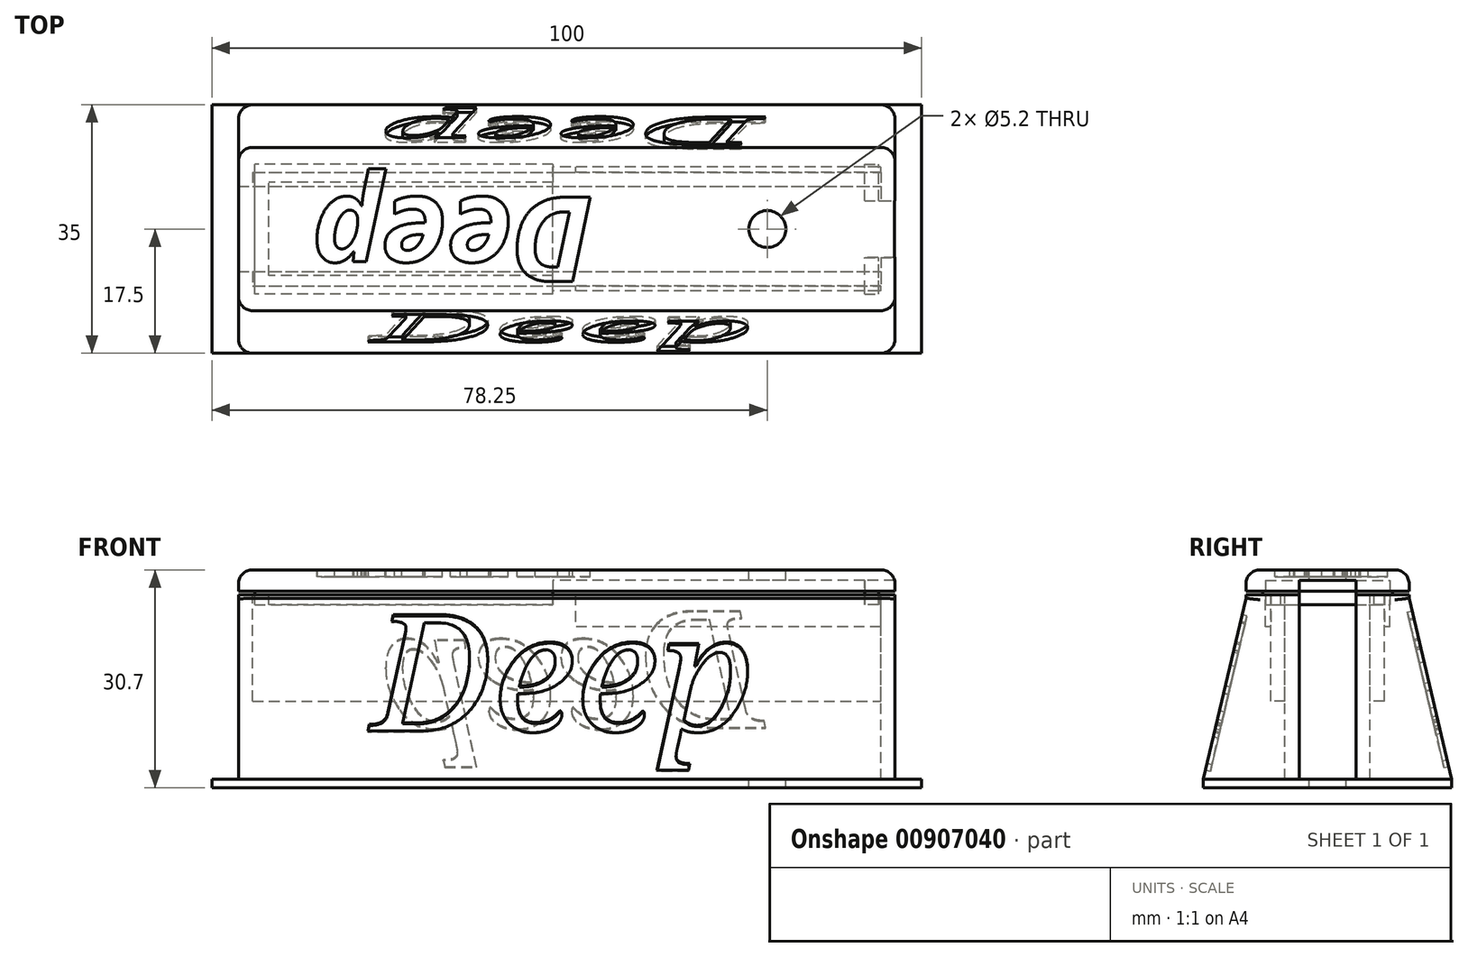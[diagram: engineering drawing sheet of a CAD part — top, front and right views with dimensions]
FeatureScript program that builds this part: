
annotation { "Feature Type Name" : "Feature", "Feature Type Description" : "" }
export const myFeature = defineFeature(function(context is Context, id is Id, definition is map)
    precondition{}
    {
        {
            var Q0;
            Q0=qCreatedBy(makeId("Top.planeOp"),FACE);
            var sketch = newSketch(context, id + "F0", { "sketchPlane" : qUnion([Q0])});
            skLineSegment(sketch, "E0.bottom", {"start": v(-50, 17.5) * mm, "end": v(50, 17.5) * mm});
            skLineSegment(sketch, "E0.top", {"start": v(-50, -17.5) * mm, "end": v(50, -17.5) * mm});
            skLineSegment(sketch, "E0.left", {"start": v(-50, 17.5) * mm, "end": v(-50, -17.5) * mm});
            skLineSegment(sketch, "E0.right", {"start": v(50, 17.5) * mm, "end": v(50, -17.5) * mm});
            skSolve(sketch);
        }
        {
            var Q0;
            Q0=makeQuery(id+"F0.imprint","IMPRINT",FACE,{"disambiguationData":[TD([[makeQuery(id+"F0.imprint","IMPRINT",EDGE,{"derivedFrom":sQuery(id+"F0.wireOp",EDGE,"E0.bottom")}),-1.0]])]});
            extrude(context, id + "F1", {"entities" : qUnion([Q0]), "depth" : 1.2 * mm, "offsetDistance" : 25 * mm});
        }
        {
            var Q0;
            Q0=makeQuery(id+"F1.opExtrude","CAP_FACE",FACE,{"disambiguationData":[OSD([sQuery(id+"F0.wireOp",EDGE,"E0.bottom"),sQuery(id+"F0.wireOp",EDGE,"E0.top"),sQuery(id+"F0.wireOp",EDGE,"E0.left"),sQuery(id+"F0.wireOp",EDGE,"E0.right")])],"isStart":false});
            var sketch = newSketch(context, id + "F2", { "sketchPlane" : qUnion([Q0])});
            skLineSegment(sketch, "E1.bottom", {"start": v(-46.25, 11.5) * mm, "end": v(46.25, 11.5) * mm});
            skLineSegment(sketch, "E1.top", {"start": v(-46.25, -11.5) * mm, "end": v(46.25, -11.5) * mm});
            skLineSegment(sketch, "E1.left", {"start": v(-46.25, 11.5) * mm, "end": v(-46.25, -11.5) * mm});
            skLineSegment(sketch, "E1.right", {"start": v(46.25, 11.5) * mm, "end": v(46.25, -11.5) * mm});
            skSolve(sketch);
        }
        {
            var Q0;
            Q0=makeQuery(id+"F2.imprint","IMPRINT",FACE,{"disambiguationData":[TD([[makeQuery(id+"F2.imprint","IMPRINT",EDGE,{"derivedFrom":sQuery(id+"F2.wireOp",EDGE,"E1.bottom")}),-1.0]])]});
            extrude(context, id + "F3", {"entities" : qUnion([Q0]), "operationType" : NewBodyOperationType.ADD, "depth" : 26 * mm, "offsetDistance" : 25 * mm});
        }
        {
            var Q0;
            Q0=makeQuery(id+"F3.opExtrude","SWEPT_FACE",FACE,{"disambiguationData":[OSD([sQuery(id+"F2.wireOp",EDGE,"E1.left")])]});
            var sketch = newSketch(context, id + "F4", { "sketchPlane" : qUnion([Q0])});
            skLineSegment(sketch, "E2", {"start": v(-11.5, 26.7) * mm, "end": v(-11.5, 1.2) * mm});
            skLineSegment(sketch, "E3", {"start": v(-11.5, 1.2) * mm, "end": v(-17.5, 1.2) * mm});
            skLineSegment(sketch, "E4", {"start": v(-17.5, 1.2) * mm, "end": v(-11.5, 26.7) * mm});
            skLineSegment(sketch, "E5", {"start": v(11.5, 26.7) * mm, "end": v(11.5, 1.2) * mm});
            skLineSegment(sketch, "E6", {"start": v(11.5, 1.2) * mm, "end": v(17.5, 1.2) * mm});
            skLineSegment(sketch, "E7", {"start": v(17.5, 1.2) * mm, "end": v(11.5, 26.7) * mm});
            skSolve(sketch);
        }
        {
            var Q0;
            Q0=makeQuery(id+"F4.imprint","IMPRINT",FACE,{"disambiguationData":[TD([[makeQuery(id+"F4.imprint","IMPRINT",EDGE,{"derivedFrom":sQuery(id+"F4.wireOp",EDGE,"E2")}),-1.0]])]});
            var Q1;
            Q1=makeQuery(id+"F4.imprint","IMPRINT",FACE,{"disambiguationData":[TD([[makeQuery(id+"F4.imprint","IMPRINT",EDGE,{"derivedFrom":sQuery(id+"F4.wireOp",EDGE,"E5")}),1.0]])]});
            extrude(context, id + "F5", {"entities" : qUnion([Q0, Q1]), "operationType" : NewBodyOperationType.ADD, "oppositeDirection" : true, "depth" : 92.5 * mm, "offsetDistance" : 25 * mm});
        }
        {
            var Q0;
            Q0=makeQuery(id+"F3.opExtrude","CAP_FACE",FACE,{"disambiguationData":[OSD([sQuery(id+"F2.wireOp",EDGE,"E1.bottom"),sQuery(id+"F2.wireOp",EDGE,"E1.top"),sQuery(id+"F2.wireOp",EDGE,"E1.left"),sQuery(id+"F2.wireOp",EDGE,"E1.right")])],"isStart":false});
            var sketch = newSketch(context, id + "F6", { "sketchPlane" : qUnion([Q0])});
            skLineSegment(sketch, "E8.bottom", {"start": v(-44.25, 8) * mm, "end": v(44.25, 8) * mm});
            skLineSegment(sketch, "E8.top", {"start": v(-44.25, -8) * mm, "end": v(44.25, -8) * mm});
            skLineSegment(sketch, "E8.left", {"start": v(-44.25, 8) * mm, "end": v(-44.25, -8) * mm});
            skLineSegment(sketch, "E8.right", {"start": v(44.25, 8) * mm, "end": v(44.25, -8) * mm});
            skSolve(sketch);
        }
        {
            var Q0;
            Q0=makeQuery(id+"F6.imprint","IMPRINT",FACE,{"disambiguationData":[TD([[makeQuery(id+"F6.imprint","IMPRINT",EDGE,{"derivedFrom":sQuery(id+"F6.wireOp",EDGE,"E8.bottom")}),-1.0]])]});
            extrude(context, id + "F7", {"entities" : qUnion([Q0]), "operationType" : NewBodyOperationType.REMOVE, "oppositeDirection" : true, "depth" : 15 * mm, "offsetDistance" : 25 * mm});
        }
        {
            var Q0;
            Q0=makeQuery(id+"F7.boolean.opBoolean","COPY",FACE,{"derivedFrom":makeQuery(id+"F7.opExtrude","CAP_FACE",FACE,{"disambiguationData":[OSD([sQuery(id+"F6.wireOp",EDGE,"E8.bottom"),sQuery(id+"F6.wireOp",EDGE,"E8.top"),sQuery(id+"F6.wireOp",EDGE,"E8.left"),sQuery(id+"F6.wireOp",EDGE,"E8.right")])],"isStart":false})});
            var sketch = newSketch(context, id + "F8", { "sketchPlane" : qUnion([Q0])});
            skLineSegment(sketch, "E9.bottom", {"start": v(-44.25, 6) * mm, "end": v(44.25, 6) * mm});
            skLineSegment(sketch, "E9.top", {"start": v(-44.25, -6) * mm, "end": v(44.25, -6) * mm});
            skLineSegment(sketch, "E9.left", {"start": v(-44.25, 6) * mm, "end": v(-44.25, -6) * mm});
            skLineSegment(sketch, "E9.right", {"start": v(44.25, 6) * mm, "end": v(44.25, -6) * mm});
            skSolve(sketch);
        }
        {
            var Q0;
            Q0=makeQuery(id+"F8.imprint","IMPRINT",FACE,{"disambiguationData":[TD([[makeQuery(id+"F8.imprint","IMPRINT",EDGE,{"derivedFrom":sQuery(id+"F8.wireOp",EDGE,"E9.bottom")}),-1.0]])]});
            extrude(context, id + "F9", {"entities" : qUnion([Q0]), "operationType" : NewBodyOperationType.REMOVE, "oppositeDirection" : true, "depth" : 11 * mm, "offsetDistance" : 25 * mm});
        }
        {
            var Q0;
            Q0=makeQuery(id+"F3.opExtrude","CAP_FACE",FACE,{"disambiguationData":[OSD([sQuery(id+"F2.wireOp",EDGE,"E1.bottom"),sQuery(id+"F2.wireOp",EDGE,"E1.top"),sQuery(id+"F2.wireOp",EDGE,"E1.left"),sQuery(id+"F2.wireOp",EDGE,"E1.right")])],"isStart":false});
            var sketch = newSketch(context, id + "F10", { "sketchPlane" : qUnion([Q0])});
            skLineSegment(sketch, "E10.bottom", {"start": v(44.25, 4) * mm, "end": v(46.25, 4) * mm});
            skLineSegment(sketch, "E10.top", {"start": v(44.25, -4) * mm, "end": v(46.25, -4) * mm});
            skLineSegment(sketch, "E10.left", {"start": v(44.25, 4) * mm, "end": v(44.25, -4) * mm});
            skLineSegment(sketch, "E10.right", {"start": v(46.25, 4) * mm, "end": v(46.25, -4) * mm});
            skSolve(sketch);
        }
        {
            var Q0;
            Q0=makeQuery(id+"F10.imprint","IMPRINT",FACE,{"disambiguationData":[TD([[makeQuery(id+"F10.imprint","IMPRINT",EDGE,{"derivedFrom":sQuery(id+"F10.wireOp",EDGE,"E10.bottom")}),-1.0]])]});
            extrude(context, id + "F11", {"entities" : qUnion([Q0]), "operationType" : NewBodyOperationType.REMOVE, "oppositeDirection" : true, "depth" : 26 * mm, "offsetDistance" : 25 * mm});
        }
        {
            var Q0;
            Q0=makeQuery(id+"F3.opExtrude","CAP_FACE",FACE,{"disambiguationData":[OSD([sQuery(id+"F2.wireOp",EDGE,"E1.bottom"),sQuery(id+"F2.wireOp",EDGE,"E1.top"),sQuery(id+"F2.wireOp",EDGE,"E1.left"),sQuery(id+"F2.wireOp",EDGE,"E1.right")])],"isStart":false});
            var sketch = newSketch(context, id + "F12", { "sketchPlane" : qUnion([Q0])});
            skLineSegment(sketch, "E11.bottom", {"start": v(-46.25, 6) * mm, "end": v(-44.25, 6) * mm});
            skLineSegment(sketch, "E11.top", {"start": v(-46.25, -6) * mm, "end": v(-44.25, -6) * mm});
            skLineSegment(sketch, "E11.left", {"start": v(-46.25, 6) * mm, "end": v(-46.25, -6) * mm});
            skLineSegment(sketch, "E11.right", {"start": v(-44.25, 6) * mm, "end": v(-44.25, -6) * mm});
            skSolve(sketch);
        }
        {
            var Q0;
            Q0=makeQuery(id+"F12.imprint","IMPRINT",FACE,{"disambiguationData":[TD([[makeQuery(id+"F12.imprint","IMPRINT",EDGE,{"derivedFrom":sQuery(id+"F12.wireOp",EDGE,"E11.bottom")}),-1.0]])]});
            extrude(context, id + "F13", {"entities" : qUnion([Q0]), "operationType" : NewBodyOperationType.REMOVE, "oppositeDirection" : true, "depth" : 26 * mm, "offsetDistance" : 25 * mm});
        }
        {
            var Q0;
            {var subQ0=sQuery(id+"F2.wireOp",EDGE,"E1.right");var subQ1=sQuery(id+"F2.wireOp",EDGE,"E1.left");var subQ2=sQuery(id+"F2.wireOp",EDGE,"E1.top");Q0=makeQuery(id+"F13.boolean.opBoolean","SPLIT",FACE,{"disambiguationData":[TD([makeQuery(id+"F3.opExtrude","SWEPT_FACE",FACE,{"disambiguationData":[OSD([subQ2])]})])],"derivedFrom":makeQuery(id+"F3.opExtrude","CAP_FACE",FACE,{"disambiguationData":[OSD([sQuery(id+"F2.wireOp",EDGE,"E1.bottom"),subQ2,subQ1,subQ0])],"isStart":false})});}
            var sketch = newSketch(context, id + "F14", { "sketchPlane" : qUnion([Q0])});
            skLineSegment(sketch, "E12.bottom", {"start": v(44.23, -8.75) * mm, "end": v(1.23, -8.75) * mm});
            skLineSegment(sketch, "E12.top", {"start": v(44.23, 8.75) * mm, "end": v(1.23, 8.75) * mm});
            skLineSegment(sketch, "E12.left", {"start": v(44.23, 8.75) * mm, "end": v(44.23, -8.75) * mm});
            skLineSegment(sketch, "E12.right", {"start": v(1.23, 8.75) * mm, "end": v(1.23, -8.75) * mm});
            skSolve(sketch);
        }
        {
            var Q0;
            Q0=makeQuery(id+"F14.imprint","IMPRINT",FACE,{"disambiguationData":[TD([[makeQuery(id+"F14.imprint","IMPRINT",EDGE,{"derivedFrom":sQuery(id+"F14.wireOp",EDGE,"E12.bottom")}),-1.0]])]});
            var Q1;
            {var subQ0=sQuery(id+"F14.wireOp",EDGE,"E12.top");Q1=makeQuery(id+"F14.imprint","IMPRINT",FACE,{"disambiguationData":[TD([[makeQuery(id+"F14.imprint","IMPRINT",EDGE,{"derivedFrom":subQ0}),1.0]])]});}
            extrude(context, id + "F15", {"entities" : qUnion([Q0, Q1]), "operationType" : NewBodyOperationType.REMOVE, "oppositeDirection" : true, "depth" : 4.5 * mm, "offsetDistance" : 25 * mm});
        }
        {
            var Q0;
            {var subQ0=sQuery(id+"F2.wireOp",EDGE,"E1.left");var subQ1=sQuery(id+"F2.wireOp",EDGE,"E1.right");var subQ2=sQuery(id+"F2.wireOp",EDGE,"E1.bottom");Q0=makeQuery(id+"F13.boolean.opBoolean","SPLIT",FACE,{"disambiguationData":[TD([makeQuery(id+"F3.opExtrude","SWEPT_FACE",FACE,{"disambiguationData":[OSD([subQ2])]})])],"derivedFrom":makeQuery(id+"F3.opExtrude","CAP_FACE",FACE,{"disambiguationData":[OSD([subQ2,sQuery(id+"F2.wireOp",EDGE,"E1.top"),subQ0,subQ1])],"isStart":false})});}
            cPlane(context, id + "F16", {"entities" : qUnion([Q0]), "cplaneType" : CPlaneType.OFFSET, "offset" : .5 * mm, "width" : 150 * mm, "height" : 150 * mm});
        }
        {
            var Q0;
            Q0=qCreatedBy(id+"F16.planeOp",FACE);
            var sketch = newSketch(context, id + "F17", { "sketchPlane" : qUnion([Q0])});
            skLineSegment(sketch, "E13.bottom", {"start": v(-46.25, 11.5) * mm, "end": v(46.25, 11.5) * mm});
            skLineSegment(sketch, "E13.top", {"start": v(-46.25, -11.5) * mm, "end": v(46.25, -11.5) * mm});
            skLineSegment(sketch, "E13.left", {"start": v(-46.25, 11.5) * mm, "end": v(-46.25, -11.5) * mm});
            skLineSegment(sketch, "E13.right", {"start": v(46.25, 11.5) * mm, "end": v(46.25, -11.5) * mm});
            skSolve(sketch);
        }
        {
            var Q0;
            Q0=makeQuery(id+"F17.imprint","IMPRINT",FACE,{"disambiguationData":[TD([[makeQuery(id+"F17.imprint","IMPRINT",EDGE,{"derivedFrom":sQuery(id+"F17.wireOp",EDGE,"E13.bottom")}),-1.0]])]});
            extrude(context, id + "F18", {"entities" : qUnion([Q0]), "depth" : 3 * mm, "offsetDistance" : 25 * mm});
        }
        {
            var Q0;
            Q0=makeQuery(id+"F18.opExtrude","SWEPT_EDGE",EDGE,{"disambiguationData":[OSD([sQuery(id+"F17.wireOp",EDGE,"E13.top"),sQuery(id+"F17.wireOp",EDGE,"E13.left")])]});
            var Q1;
            Q1=makeQuery(id+"F18.opExtrude","CAP_EDGE",EDGE,{"disambiguationData":[OSD([sQuery(id+"F17.wireOp",EDGE,"E13.left")])],"isStart":false});
            var Q2;
            Q2=makeQuery(id+"F18.opExtrude","CAP_EDGE",EDGE,{"disambiguationData":[OSD([sQuery(id+"F17.wireOp",EDGE,"E13.top")])],"isStart":false});
            var Q3;
            Q3=makeQuery(id+"F18.opExtrude","SWEPT_EDGE",EDGE,{"disambiguationData":[OSD([sQuery(id+"F17.wireOp",EDGE,"E13.top"),sQuery(id+"F17.wireOp",EDGE,"E13.right")])]});
            var Q4;
            Q4=makeQuery(id+"F18.opExtrude","CAP_EDGE",EDGE,{"disambiguationData":[OSD([sQuery(id+"F17.wireOp",EDGE,"E13.right")])],"isStart":false});
            var Q5;
            Q5=makeQuery(id+"F18.opExtrude","SWEPT_EDGE",EDGE,{"disambiguationData":[OSD([sQuery(id+"F17.wireOp",EDGE,"E13.bottom"),sQuery(id+"F17.wireOp",EDGE,"E13.right")])]});
            var Q6;
            Q6=makeQuery(id+"F18.opExtrude","CAP_EDGE",EDGE,{"disambiguationData":[OSD([sQuery(id+"F17.wireOp",EDGE,"E13.bottom")])],"isStart":false});
            var Q7;
            Q7=makeQuery(id+"F18.opExtrude","SWEPT_EDGE",EDGE,{"disambiguationData":[OSD([sQuery(id+"F17.wireOp",EDGE,"E13.bottom"),sQuery(id+"F17.wireOp",EDGE,"E13.left")])]});
            fillet(context, id + "F19", {"entities" : qUnion([Q0, Q1, Q2, Q3, Q4, Q5, Q6, Q7]), "radius" : 2 * mm, "tangentPropagation" : true, "allowEdgeOverflow" : false});
        }
        {
            var Q0;
            Q0=makeQuery(id+"F5.opExtrude","SWEPT_FACE",FACE,{"disambiguationData":[OSD([sQuery(id+"F4.wireOp",EDGE,"E7")])]});
            var sketch = newSketch(context, id + "F20", { "sketchPlane" : qUnion([Q0])});
            skText(sketch, "E14", { "text": "Deep", "fontName": "NotoSerif-Italic.ttf"});
            const initialGuessF20  = {"E14": [-0.0275, 0.00413, 1, 0, 0.01699]};
            skSetInitialGuess(sketch, initialGuessF20);
            skSolve(sketch);
        }
        {
            var Q0;
            Q0 = qSketchRegion(id + "F20", true);
            extrude(context, id + "F21", {"entities" : qUnion([Q0]), "operationType" : NewBodyOperationType.REMOVE, "oppositeDirection" : true, "depth" : .7 * mm, "offsetDistance" : 25 * mm});
        }
        {
            var Q0;
            Q0=makeQuery(id+"F5.opExtrude","SWEPT_FACE",FACE,{"disambiguationData":[OSD([sQuery(id+"F4.wireOp",EDGE,"E4")])]});
            var sketch = newSketch(context, id + "F22", { "sketchPlane" : qUnion([Q0])});
            skText(sketch, "E15", { "text": "Deep", "fontName": "NotoSerif-Italic.ttf"});
            const initialGuessF22  = {"E15": [-0.0275, 0.00468, 1, 0, 0.01699]};
            skSetInitialGuess(sketch, initialGuessF22);
            skSolve(sketch);
        }
        {
            var Q0;
            Q0 = qSketchRegion(id + "F22", true);
            extrude(context, id + "F23", {"entities" : qUnion([Q0]), "operationType" : NewBodyOperationType.REMOVE, "oppositeDirection" : true, "depth" : .7 * mm, "offsetDistance" : 25 * mm});
        }
        {
            var Q0;
            Q0=makeQuery(id+"F5.opExtrude","CAP_EDGE",EDGE,{"disambiguationData":[OSD([sQuery(id+"F4.wireOp",EDGE,"E4")])],"isStart":false});
            var Q1;
            Q1=makeQuery(id+"F5.opExtrude","CAP_EDGE",EDGE,{"disambiguationData":[OSD([sQuery(id+"F4.wireOp",EDGE,"E7")])],"isStart":false});
            var Q2;
            Q2=makeQuery(id+"F5.opExtrude","CAP_EDGE",EDGE,{"disambiguationData":[OSD([sQuery(id+"F4.wireOp",EDGE,"E7")])],"isStart":true});
            var Q3;
            Q3=makeQuery(id+"F5.opExtrude","CAP_EDGE",EDGE,{"disambiguationData":[OSD([sQuery(id+"F4.wireOp",EDGE,"E4")])],"isStart":true});
            var Q4;
            Q4=makeQuery(id+"F3.opExtrude","SWEPT_EDGE",EDGE,{"disambiguationData":[OSD([sQuery(id+"F2.wireOp",EDGE,"E1.bottom"),sQuery(id+"F2.wireOp",EDGE,"E1.right")])]});
            var Q5;
            Q5=makeQuery(id+"F3.opExtrude","SWEPT_EDGE",EDGE,{"disambiguationData":[OSD([sQuery(id+"F2.wireOp",EDGE,"E1.top"),sQuery(id+"F2.wireOp",EDGE,"E1.right")])]});
            var Q6;
            Q6=makeQuery(id+"F3.opExtrude","SWEPT_EDGE",EDGE,{"disambiguationData":[OSD([sQuery(id+"F2.wireOp",EDGE,"E1.top"),sQuery(id+"F2.wireOp",EDGE,"E1.left")])]});
            var Q7;
            Q7=makeQuery(id+"F3.opExtrude","SWEPT_EDGE",EDGE,{"disambiguationData":[OSD([sQuery(id+"F2.wireOp",EDGE,"E1.bottom"),sQuery(id+"F2.wireOp",EDGE,"E1.left")])]});
            fillet(context, id + "F24", {"entities" : qUnion([Q0, Q1, Q2, Q3, Q4, Q5, Q6, Q7]), "radius" : 2 * mm, "tangentPropagation" : true, "allowEdgeOverflow" : false});
        }
        {
            var Q0;
            Q0=makeQuery(id+"F18.opExtrude","CAP_FACE",FACE,{"disambiguationData":[OSD([sQuery(id+"F17.wireOp",EDGE,"E13.bottom"),sQuery(id+"F17.wireOp",EDGE,"E13.top"),sQuery(id+"F17.wireOp",EDGE,"E13.left"),sQuery(id+"F17.wireOp",EDGE,"E13.right")])],"isStart":true});
            var sketch = newSketch(context, id + "F25", { "sketchPlane" : qUnion([Q0])});
            skLineSegment(sketch, "E16.bottom", {"start": v(41.95, 9.15) * mm, "end": v(43.95, 9.15) * mm});
            skLineSegment(sketch, "E16.top", {"start": v(41.95, 4) * mm, "end": v(43.95, 4) * mm});
            skLineSegment(sketch, "E16.left", {"start": v(41.95, 9.15) * mm, "end": v(41.95, 4) * mm});
            skLineSegment(sketch, "E16.right", {"start": v(43.95, 9.15) * mm, "end": v(43.95, 4) * mm});
            skLineSegment(sketch, "E17.bottom", {"start": v(41.95, -4) * mm, "end": v(43.95, -4) * mm});
            skLineSegment(sketch, "E17.top", {"start": v(41.95, -9.15) * mm, "end": v(43.95, -9.15) * mm});
            skLineSegment(sketch, "E17.left", {"start": v(41.95, -4) * mm, "end": v(41.95, -9.15) * mm});
            skLineSegment(sketch, "E17.right", {"start": v(43.95, -4) * mm, "end": v(43.95, -9.15) * mm});
            skPoint(sketch, "E18.oppositeSnap0", {"position": v(41.95, 6.57) * mm});
            skLineSegment(sketch, "E18.bottom", {"start": v(-1.95, 9.15) * mm, "end": v(-43.95, 9.15) * mm});
            skLineSegment(sketch, "E18.top", {"start": v(-1.95, 6.57) * mm, "end": v(-43.95, 6.57) * mm});
            skLineSegment(sketch, "E18.left", {"start": v(-1.95, 9.15) * mm, "end": v(-1.95, 6.57) * mm});
            skLineSegment(sketch, "E18.right", {"start": v(-43.95, 9.15) * mm, "end": v(-43.95, 6.57) * mm});
            skPoint(sketch, "E19.oppositeSnap0", {"position": v(43.95, -6.57) * mm});
            skLineSegment(sketch, "E19.bottom", {"start": v(-1.95, -9.15) * mm, "end": v(-43.95, -9.15) * mm});
            skLineSegment(sketch, "E19.top", {"start": v(-1.95, -6.57) * mm, "end": v(-43.95, -6.58) * mm});
            skLineSegment(sketch, "E19.left", {"start": v(-1.95, -9.15) * mm, "end": v(-1.95, -6.57) * mm});
            skLineSegment(sketch, "E19.right", {"start": v(-43.95, -9.15) * mm, "end": v(-43.95, -6.57) * mm});
            skLineSegment(sketch, "E20.bottom", {"start": v(-43.95, 6.57) * mm, "end": v(-41.95, 6.57) * mm});
            skLineSegment(sketch, "E20.top", {"start": v(-43.95, -6.58) * mm, "end": v(-41.95, -6.58) * mm});
            skLineSegment(sketch, "E20.left", {"start": v(-43.95, 6.57) * mm, "end": v(-43.95, -6.57) * mm});
            skLineSegment(sketch, "E20.right", {"start": v(-41.95, 6.57) * mm, "end": v(-41.95, -6.58) * mm});
            skSolve(sketch);
        }
        {
            var Q0;
            Q0=makeQuery(id+"F25.imprint","IMPRINT",FACE,{"disambiguationData":[TD([[makeQuery(id+"F25.imprint","IMPRINT",EDGE,{"derivedFrom":sQuery(id+"F25.wireOp",EDGE,"E18.bottom")}),1.0]])]});
            var Q1;
            {var subQ0=sQuery(id+"F25.wireOp",EDGE,"E20.left");Q1=makeQuery(id+"F25.imprint","IMPRINT",FACE,{"disambiguationData":[TD([[makeQuery(id+"F25.imprint","IMPRINT",EDGE,{"derivedFrom":subQ0}),1.0]])]});}
            var Q2;
            Q2=makeQuery(id+"F25.imprint","IMPRINT",FACE,{"disambiguationData":[TD([[makeQuery(id+"F25.imprint","IMPRINT",EDGE,{"derivedFrom":sQuery(id+"F25.wireOp",EDGE,"E19.bottom")}),-1.0]])]});
            var Q3;
            Q3=makeQuery(id+"F25.imprint","IMPRINT",FACE,{"disambiguationData":[TD([[makeQuery(id+"F25.imprint","IMPRINT",EDGE,{"derivedFrom":sQuery(id+"F25.wireOp",EDGE,"E16.bottom")}),-1.0]])]});
            var Q4;
            Q4=makeQuery(id+"F25.imprint","IMPRINT",FACE,{"disambiguationData":[TD([[makeQuery(id+"F25.imprint","IMPRINT",EDGE,{"derivedFrom":sQuery(id+"F25.wireOp",EDGE,"E17.bottom")}),-1.0]])]});
            extrude(context, id + "F26", {"entities" : qUnion([Q0, Q1, Q2, Q3, Q4]), "operationType" : NewBodyOperationType.ADD, "depth" : 1.9 * mm, "offsetDistance" : 25 * mm});
        }
        {
            var Q0;
            Q0=makeQuery(id+"F18.opExtrude","CAP_FACE",FACE,{"disambiguationData":[OSD([sQuery(id+"F17.wireOp",EDGE,"E13.bottom"),sQuery(id+"F17.wireOp",EDGE,"E13.top"),sQuery(id+"F17.wireOp",EDGE,"E13.left"),sQuery(id+"F17.wireOp",EDGE,"E13.right")])],"isStart":false});
            var sketch = newSketch(context, id + "F27", { "sketchPlane" : qUnion([Q0])});
            skCircle(sketch, "E21", {"center": v(28.25, 0) * mm, "radius": 2.6 * mm});
            skSolve(sketch);
        }
        {
            var Q0;
            Q0=makeQuery(id+"F27.imprint","IMPRINT",FACE,{"disambiguationData":[TD([[makeQuery(id+"F27.imprint","IMPRINT",EDGE,{"derivedFrom":sQuery(id+"F27.wireOp",EDGE,"E21")}),1.0]])]});
            extrude(context, id + "F28", {"entities" : qUnion([Q0]), "operationType" : NewBodyOperationType.REMOVE, "endBound" : BoundingType.THROUGH_ALL, "oppositeDirection" : true, "depth" : 25 * mm, "offsetDistance" : 25 * mm});
        }
        {
            var Q0;
            Q0=makeQuery(id+"F18.opExtrude","CAP_FACE",FACE,{"disambiguationData":[OSD([sQuery(id+"F17.wireOp",EDGE,"E13.bottom"),sQuery(id+"F17.wireOp",EDGE,"E13.top"),sQuery(id+"F17.wireOp",EDGE,"E13.left"),sQuery(id+"F17.wireOp",EDGE,"E13.right")])],"isStart":false});
            var sketch = newSketch(context, id + "F29", { "sketchPlane" : qUnion([Q0])});
            skText(sketch, "E22", { "text": "Deep", "fontName": "OpenSans-BoldItalic.ttf"});
            skPoint(sketch, "E23", {"position": v(-44.25, -7.5) * mm});
            const initialGuessF29  = {"E22": [0.00375, 0.00447, -1, 0, 0.01197]};
            skSetInitialGuess(sketch, initialGuessF29);
            skSolve(sketch);
        }
        {
            var Q0;
            Q0 = qSketchRegion(id + "F29", true);
            extrude(context, id + "F30", {"entities" : qUnion([Q0]), "operationType" : NewBodyOperationType.REMOVE, "oppositeDirection" : true, "depth" : 1 * mm, "offsetDistance" : 25 * mm});
        }
        {
            var Q0;
            Q0=makeQuery(id+"F18.opExtrude","CAP_FACE",FACE,{"disambiguationData":[OSD([sQuery(id+"F17.wireOp",EDGE,"E13.bottom"),sQuery(id+"F17.wireOp",EDGE,"E13.top"),sQuery(id+"F17.wireOp",EDGE,"E13.left"),sQuery(id+"F17.wireOp",EDGE,"E13.right")])],"isStart":true});
            var sketch = newSketch(context, id + "F31", { "sketchPlane" : qUnion([Q0])});
            skLineSegment(sketch, "E24.bottom", {"start": v(46.25, 4) * mm, "end": v(36.25, 4) * mm});
            skLineSegment(sketch, "E24.top", {"start": v(46.25, -4) * mm, "end": v(36.25, -4) * mm});
            skLineSegment(sketch, "E24.left", {"start": v(46.25, 4) * mm, "end": v(46.25, -4) * mm});
            skLineSegment(sketch, "E24.right", {"start": v(36.25, 4) * mm, "end": v(36.25, -4) * mm});
            skLineSegment(sketch, "E25.bottom", {"start": v(41.95, -8.75) * mm, "end": v(-1.95, -8.75) * mm});
            skLineSegment(sketch, "E25.top", {"start": v(41.95, 8.75) * mm, "end": v(-1.95, 8.75) * mm});
            skLineSegment(sketch, "E25.left", {"start": v(41.95, -8.75) * mm, "end": v(41.95, 8.75) * mm});
            skLineSegment(sketch, "E25.right", {"start": v(-1.95, -8.75) * mm, "end": v(-1.95, 8.75) * mm});
            skSolve(sketch);
        }
        {
            var Q0;
            {var subQ4=sQuery(id+"F31.wireOp",EDGE,"E24.left");Q0=makeQuery(id+"F31.imprint","IMPRINT",FACE,{"disambiguationData":[TD([[makeQuery(id+"F31.imprint","IMPRINT",EDGE,{"derivedFrom":subQ4}),1.0]])]});}
            var Q1;
            {var subQ3=sQuery(id+"F31.wireOp",EDGE,"E24.right");Q1=makeQuery(id+"F31.imprint","IMPRINT",FACE,{"disambiguationData":[TD([[makeQuery(id+"F31.imprint","IMPRINT",EDGE,{"derivedFrom":subQ3}),1.0]])]});}
            var Q2;
            {var subQ10=sQuery(id+"F31.wireOp",EDGE,"E24.right");Q2=makeQuery(id+"F31.imprint","IMPRINT",FACE,{"disambiguationData":[TD([[makeQuery(id+"F31.imprint","IMPRINT",EDGE,{"derivedFrom":subQ10}),-1.0]])]});}
            extrude(context, id + "F32", {"entities" : qUnion([Q0, Q1, Q2]), "operationType" : NewBodyOperationType.REMOVE, "oppositeDirection" : true, "depth" : 1.5 * mm, "offsetDistance" : 25 * mm});
        }
    });
